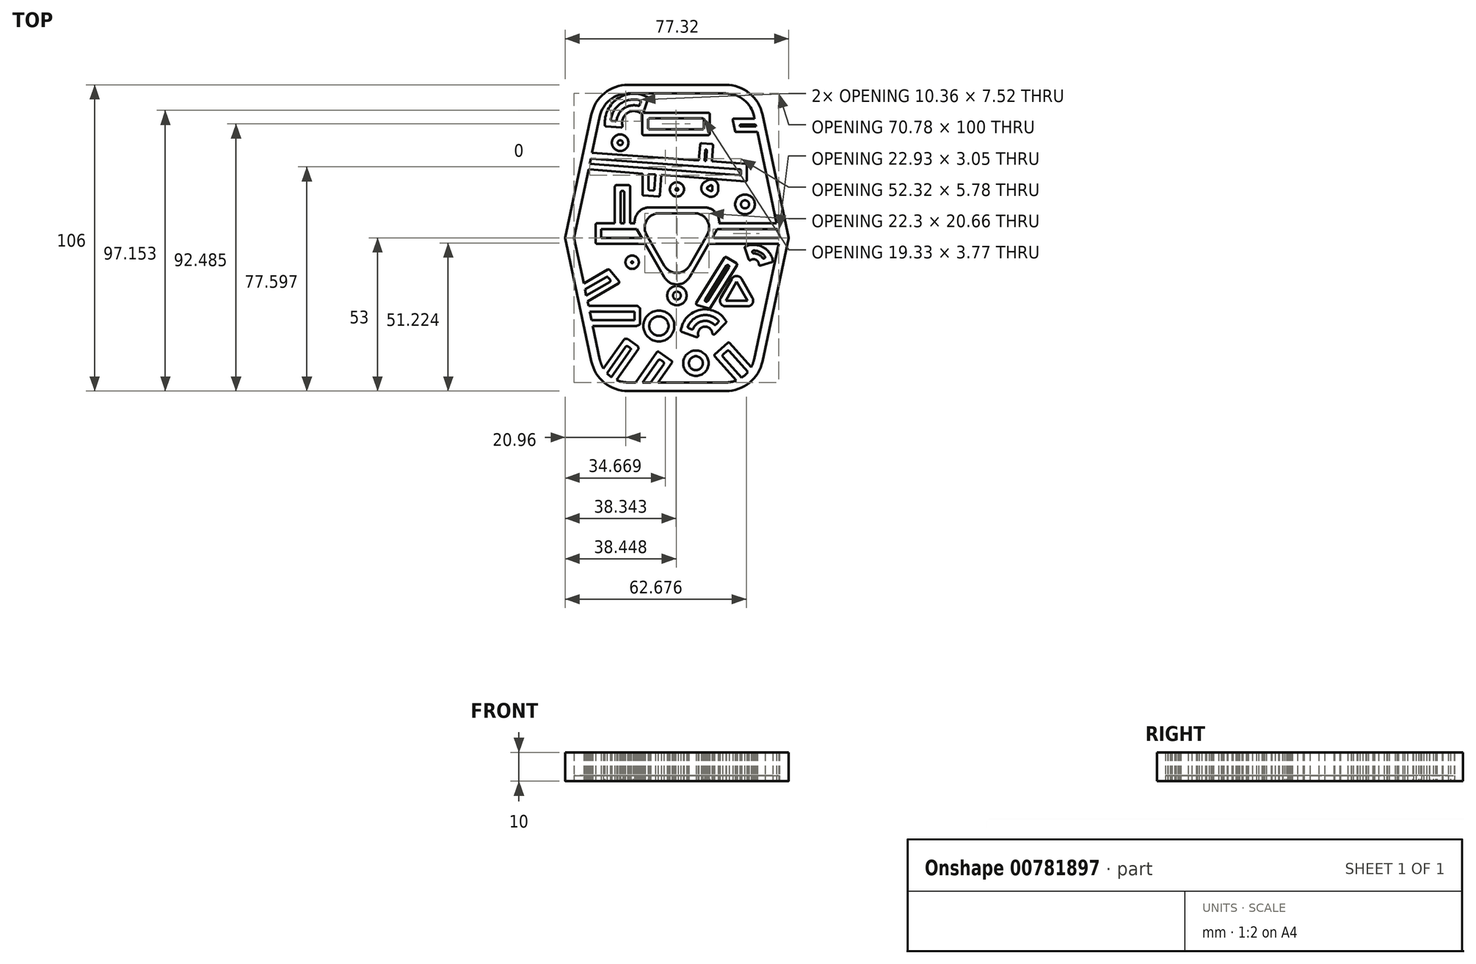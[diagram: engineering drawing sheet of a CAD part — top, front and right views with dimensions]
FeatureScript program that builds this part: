
annotation { "Feature Type Name" : "Feature", "Feature Type Description" : "" }
export const myFeature = defineFeature(function(context is Context, id is Id, definition is map)
    precondition{}
    {
        {
            var Q0;
            Q0=qCreatedBy(makeId("Top.planeOp"),FACE);
            var sketch = newSketch(context, id + "F0", { "sketchPlane" : qUnion([Q0])});
            skPoint(sketch, "E0.orphan", {"position": v(35.6, 0) * mm});
            skPoint(sketch, "E1.visualSharp", {"position": v(35, 0) * mm});
            skPoint(sketch, "E2.visualSharp", {"position": v(-41.06, 0) * mm});
            skArc(sketch, "E3", {"start": v(12.85, -29.92) * mm, "mid": v(8.9, -28.77) * mm, "end": v(5.69, -31.32) * mm});
            skArc(sketch, "E4.0", {"start": v(14.24, -28.47) * mm, "mid": v(8.49, -26.81) * mm, "end": v(3.83, -30.58) * mm});
            skLineSegment(sketch, "E5", {"start": v(4.12, -31.25) * mm, "end": v(5.06, -31.59) * mm});
            skLineSegment(sketch, "E6", {"start": v(14.25, -29.18) * mm, "end": v(13.56, -29.9) * mm});
            skCircle(sketch, "E7.cCircle", {"center": v(0, 0) * mm, "radius": 8.55 * mm, "construction": true});
            skLineSegment(sketch, "E7.0", {"start": v(-6.15, 8.55) * mm, "end": v(6.15, 8.55) * mm});
            skLineSegment(sketch, "E7.1", {"start": v(10.48, 1.05) * mm, "end": v(4.33, -9.6) * mm});
            skLineSegment(sketch, "E7.2", {"start": v(-4.33, -9.6) * mm, "end": v(-10.48, 1.05) * mm});
            skPoint(sketch, "E7.0.midPoint", {"position": v(0, 8.55) * mm});
            skLineSegment(sketch, "E8.0", {"start": v(-9.62, 10.55) * mm, "end": v(9.62, 10.55) * mm});
            skLineSegment(sketch, "E8.1", {"start": v(-4.33, -13.6) * mm, "end": v(-11.03, -2) * mm});
            skLineSegment(sketch, "E8.2", {"start": v(13.8, 2.8) * mm, "end": v(12.62, 0.75) * mm});
            skLineSegment(sketch, "E9", {"start": v(-29.56, -28.5) * mm, "end": v(-14.73, -28.5) * mm});
            skLineSegment(sketch, "E10", {"start": v(-14.73, -28.5) * mm, "end": v(-14.73, -25.54) * mm});
            skLineSegment(sketch, "E11", {"start": v(-14.73, -25.54) * mm, "end": v(-30.19, -25.54) * mm});
            skLineSegment(sketch, "E12.0", {"start": v(-14.73, -23.54) * mm, "end": v(-30.6, -23.54) * mm});
            skLineSegment(sketch, "E13.0", {"start": v(-12.73, -29.9) * mm, "end": v(-12.73, -25.66) * mm});
            skLineSegment(sketch, "E13.1", {"start": v(-29.14, -30.5) * mm, "end": v(-14.16, -30.5) * mm});
            skLineSegment(sketch, "E14", {"start": v(-14.73, -23.54) * mm, "end": v(-13.63, -23.54) * mm});
            skLineSegment(sketch, "E15", {"start": v(-12.76, -24.33) * mm, "end": v(-12.73, -25.66) * mm});
            skArc(sketch, "E16", {"start": v(-12.76, -24.33) * mm, "mid": v(-13.17, -23.91) * mm, "end": v(-13.63, -23.54) * mm});
            skArc(sketch, "E17", {"start": v(-14.16, -30.5) * mm, "mid": v(-13.43, -30.24) * mm, "end": v(-12.73, -29.9) * mm});
            skPoint(sketch, "E18.visualSharp", {"position": v(0, -21.1) * mm});
            skArc(sketch, "E18.filletArc", {"start": v(-4.33, -13.6) * mm, "mid": v(0, -16.1) * mm, "end": v(4.33, -13.6) * mm});
            skPoint(sketch, "E19.visualSharp", {"position": v(0, -17.1) * mm});
            skArc(sketch, "E19.filletArc", {"start": v(-4.33, -9.6) * mm, "mid": v(0, -12.1) * mm, "end": v(4.33, -9.6) * mm});
            skArc(sketch, "E20.filletArc", {"start": v(14.6, 5.05) * mm, "mid": v(13.32, 8.9) * mm, "end": v(9.62, 10.55) * mm});
            skArc(sketch, "E21.filletArc", {"start": v(10.48, 1.05) * mm, "mid": v(10.48, 6.05) * mm, "end": v(6.15, 8.55) * mm});
            skArc(sketch, "E22.filletArc", {"start": v(-9.62, 10.55) * mm, "mid": v(-13.32, 8.9) * mm, "end": v(-14.6, 5.05) * mm});
            skArc(sketch, "E23.filletArc", {"start": v(-6.15, 8.55) * mm, "mid": v(-10.48, 6.05) * mm, "end": v(-10.48, 1.05) * mm});
            skPoint(sketch, "E24.2.start.orphan", {"position": v(-16, 68.56) * mm});
            skLineSegment(sketch, "E25", {"start": v(-13.95, 3.05) * mm, "end": v(-26.18, 3.05) * mm});
            skLineSegment(sketch, "E26", {"start": v(-12.18, 0) * mm, "end": v(-28.18, 0) * mm});
            skLineSegment(sketch, "E27.0", {"start": v(-14.6, 5.05) * mm, "end": v(-16.21, 5.05) * mm});
            skLineSegment(sketch, "E28.0", {"start": v(-12.18, -2) * mm, "end": v(-27.68, -2) * mm});
            skLineSegment(sketch, "E29", {"start": v(-12.18, -2) * mm, "end": v(-11.03, -2) * mm});
            skLineSegment(sketch, "E30", {"start": v(-58.8, 0) * mm, "end": v(-35.6, 0) * mm, "construction": true});
            skLineSegment(sketch, "E31", {"start": v(0, 47.65) * mm, "end": v(0, -85.38) * mm, "construction": true});
            skLineSegment(sketch, "E32", {"start": v(26.68, -42.07) * mm, "end": v(35.18, -2) * mm});
            skLineSegment(sketch, "E33", {"start": v(16.9, -50) * mm, "end": v(0, -50) * mm});
            skPoint(sketch, "E34.visualSharp", {"position": v(25, -50) * mm});
            skArc(sketch, "E34.filletArc", {"start": v(16.9, -50) * mm, "mid": v(18.76, -49.83) * mm, "end": v(20.55, -49.3) * mm});
            skLineSegment(sketch, "E35.MirrorCS", {"start": v(-16.9, -50) * mm, "end": v(-14.28, -50) * mm});
            skArc(sketch, "E36.MirrorCS", {"start": v(-16.9, -50) * mm, "mid": v(-18.95, -49.79) * mm, "end": v(-20.92, -49.15) * mm});
            skLineSegment(sketch, "E37.MirrorCS", {"start": v(-26.68, -42.07) * mm, "end": v(-29.14, -30.5) * mm});
            skLineSegment(sketch, "E38.MirrorCS", {"start": v(26.68, 42.07) * mm, "end": v(26.84, 41.31) * mm});
            skArc(sketch, "E39.MirrorCS", {"start": v(16.9, 50) * mm, "mid": v(23.2, 47.77) * mm, "end": v(26.68, 42.07) * mm});
            skLineSegment(sketch, "E40.MirrorCS", {"start": v(16.9, 50) * mm, "end": v(0, 50) * mm});
            skLineSegment(sketch, "E41.MirrorCS", {"start": v(-16.9, 50) * mm, "end": v(0, 50) * mm});
            skArc(sketch, "E42.MirrorCS", {"start": v(-16.9, 50) * mm, "mid": v(-23.2, 47.77) * mm, "end": v(-26.68, 42.07) * mm});
            skLineSegment(sketch, "E43.MirrorCS", {"start": v(-26.68, 42.07) * mm, "end": v(-29.35, 29.46) * mm});
            skArc(sketch, "E44.0", {"start": v(-16.9, 53) * mm, "mid": v(-25.08, 50.1) * mm, "end": v(-29.62, 42.7) * mm});
            skLineSegment(sketch, "E44.1", {"start": v(29.62, -42.7) * mm, "end": v(38.64, -0.1) * mm});
            skLineSegment(sketch, "E44.2", {"start": v(29.62, 42.7) * mm, "end": v(38.64, 0.1) * mm});
            skArc(sketch, "E44.3", {"start": v(16.9, 53) * mm, "mid": v(25.08, 50.1) * mm, "end": v(29.62, 42.7) * mm});
            skLineSegment(sketch, "E44.4", {"start": v(16.9, 53) * mm, "end": v(0, 53) * mm});
            skArc(sketch, "E44.5", {"start": v(16.9, -53) * mm, "mid": v(25.08, -50.1) * mm, "end": v(29.62, -42.7) * mm});
            skLineSegment(sketch, "E44.6", {"start": v(-16.9, 53) * mm, "end": v(0, 53) * mm});
            skLineSegment(sketch, "E44.7", {"start": v(16.9, -53) * mm, "end": v(0, -53) * mm});
            skLineSegment(sketch, "E44.8", {"start": v(-16.9, -53) * mm, "end": v(0, -53) * mm});
            skArc(sketch, "E44.9", {"start": v(-16.9, -53) * mm, "mid": v(-25.08, -50.1) * mm, "end": v(-29.62, -42.7) * mm});
            skLineSegment(sketch, "E44.10", {"start": v(-29.62, -42.7) * mm, "end": v(-38.64, -0.1) * mm});
            skLineSegment(sketch, "E44.11", {"start": v(-29.62, 42.7) * mm, "end": v(-38.64, 0.1) * mm});
            skLineSegment(sketch, "E45", {"start": v(9.35, 40) * mm, "end": v(9.35, 38.1) * mm});
            skLineSegment(sketch, "E46", {"start": v(8.85, 37.6) * mm, "end": v(-9.48, 37.6) * mm});
            skLineSegment(sketch, "E47", {"start": v(-9.98, 38.1) * mm, "end": v(-9.98, 40.87) * mm});
            skLineSegment(sketch, "E48", {"start": v(-9.48, 41.37) * mm, "end": v(8.85, 41.37) * mm});
            skLineSegment(sketch, "E49", {"start": v(9.35, 40.87) * mm, "end": v(9.35, 40) * mm});
            skLineSegment(sketch, "E50", {"start": v(-22.67, -48.17) * mm, "end": v(-16.9, -40) * mm});
            skPoint(sketch, "E50.startSnap0", {"position": v(-22.67, -23.54) * mm});
            skLineSegment(sketch, "E51.1", {"start": v(-16.97, -37.5) * mm, "end": v(-16.15, -38.08) * mm});
            skLineSegment(sketch, "E51.2", {"start": v(-24.19, -46.85) * mm, "end": v(-17.66, -37.62) * mm});
            skLineSegment(sketch, "E52", {"start": v(-16.9, -40) * mm, "end": v(-16.03, -38.78) * mm});
            skLineSegment(sketch, "E53.0", {"start": v(-21.04, -49.32) * mm, "end": v(-15.26, -41.15) * mm});
            skLineSegment(sketch, "E53.1", {"start": v(-15.26, -41.15) * mm, "end": v(-13.3, -38.39) * mm});
            skLineSegment(sketch, "E53.2", {"start": v(-17.1, -34.96) * mm, "end": v(-13.52, -37.49) * mm});
            skLineSegment(sketch, "E53.3", {"start": v(-25.46, -45.17) * mm, "end": v(-18.25, -34.99) * mm});
            skLineSegment(sketch, "E54", {"start": v(-11.83, -50) * mm, "end": v(-6.41, -42.33) * mm});
            skLineSegment(sketch, "E55", {"start": v(-5.72, -42.21) * mm, "end": v(-4.67, -42.96) * mm});
            skLineSegment(sketch, "E56", {"start": v(-4.55, -43.65) * mm, "end": v(-9.04, -50) * mm});
            skLineSegment(sketch, "E57.0", {"start": v(-1.76, -43.17) * mm, "end": v(-6.59, -50) * mm});
            skLineSegment(sketch, "E57.1", {"start": v(-6.2, -39.43) * mm, "end": v(-1.88, -42.48) * mm});
            skLineSegment(sketch, "E57.2", {"start": v(-13.47, -48.85) * mm, "end": v(-6.9, -39.55) * mm});
            skLineSegment(sketch, "E58", {"start": v(-13.47, -48.85) * mm, "end": v(-14.28, -50) * mm});
            skCircle(sketch, "E59", {"center": v(-6.24, -30.45) * mm, "radius": 3.34 * mm});
            skCircle(sketch, "E60.0", {"center": v(-6.24, -30.45) * mm, "radius": 5.34 * mm});
            skArc(sketch, "E61", {"start": v(-17.1, -34.96) * mm, "mid": v(-17.68, -34.94) * mm, "end": v(-18.25, -34.99) * mm});
            skArc(sketch, "E62", {"start": v(-13.3, -38.39) * mm, "mid": v(-13.37, -37.93) * mm, "end": v(-13.52, -37.49) * mm});
            skArc(sketch, "E63.trimOffspring", {"start": v(-25.46, -45.17) * mm, "mid": v(-26.2, -43.68) * mm, "end": v(-26.68, -42.07) * mm});
            skArc(sketch, "E64.0", {"start": v(16.98, -28.7) * mm, "mid": v(8.04, -24.86) * mm, "end": v(1.38, -31.96) * mm});
            skLineSegment(sketch, "E64.1", {"start": v(16.9, -29.31) * mm, "end": v(13.1, -33.26) * mm});
            skArc(sketch, "E64.2", {"start": v(12.23, -32.96) * mm, "mid": v(9.38, -30.71) * mm, "end": v(7.36, -33.73) * mm});
            skLineSegment(sketch, "E64.3", {"start": v(1.7, -32.5) * mm, "end": v(6.7, -34.31) * mm});
            skCircle(sketch, "E65", {"center": v(6.55, -43.33) * mm, "radius": 2.4 * mm});
            skCircle(sketch, "E66.0", {"center": v(6.55, -43.33) * mm, "radius": 4.4 * mm});
            skLineSegment(sketch, "E67", {"start": v(14.24, 3.05) * mm, "end": v(34.55, 3.05) * mm});
            skLineSegment(sketch, "E68", {"start": v(-9.88, 0) * mm, "end": v(-8.55, 0) * mm});
            skLineSegment(sketch, "E69", {"start": v(-8.72, -2) * mm, "end": v(-8.31, -2) * mm});
            skLineSegment(sketch, "E70.trimOffspring", {"start": v(-9.88, 0) * mm, "end": v(-8.55, 0) * mm, "construction": true});
            skLineSegment(sketch, "E71.trimOffspring", {"start": v(14.6, 5.05) * mm, "end": v(34.53, 5.05) * mm});
            skLineSegment(sketch, "E72.trimOffspring", {"start": v(8.55, 0) * mm, "end": v(9.88, 0) * mm, "construction": true});
            skLineSegment(sketch, "E73.trimOffspring", {"start": v(8.55, 0) * mm, "end": v(9.88, 0) * mm});
            skLineSegment(sketch, "E74.trimOffspring", {"start": v(8.31, -2) * mm, "end": v(8.72, -2) * mm});
            skLineSegment(sketch, "E75.trimOffspring", {"start": v(12.18, 0) * mm, "end": v(60.57, 0) * mm, "construction": true});
            skLineSegment(sketch, "E76.trimOffspring", {"start": v(11.03, -2) * mm, "end": v(35.18, -2) * mm});
            skLineSegment(sketch, "E77.trimOffspring", {"start": v(13.05, 0) * mm, "end": v(34.98, 0) * mm});
            skLineSegment(sketch, "E78", {"start": v(22.39, -48.36) * mm, "end": v(15.9, -41.12) * mm});
            skLineSegment(sketch, "E79", {"start": v(15.94, -40.41) * mm, "end": v(17.39, -39.11) * mm});
            skLineSegment(sketch, "E80", {"start": v(18.1, -39.15) * mm, "end": v(24.58, -46.4) * mm});
            skLineSegment(sketch, "E81.0", {"start": v(18.25, -36.33) * mm, "end": v(25.73, -44.68) * mm});
            skLineSegment(sketch, "E81.1", {"start": v(13.12, -40.25) * mm, "end": v(17.55, -36.29) * mm});
            skLineSegment(sketch, "E81.2", {"start": v(20.55, -49.3) * mm, "end": v(13.08, -40.96) * mm});
            skLineSegment(sketch, "E82.0", {"start": v(11.35, 42.87) * mm, "end": v(11.35, 40) * mm});
            skLineSegment(sketch, "E82.1", {"start": v(-11.65, 43.37) * mm, "end": v(10.85, 43.37) * mm});
            skLineSegment(sketch, "E82.2", {"start": v(11.35, 40) * mm, "end": v(11.35, 36.1) * mm});
            skLineSegment(sketch, "E82.3", {"start": v(10.85, 35.6) * mm, "end": v(-11.48, 35.6) * mm});
            skLineSegment(sketch, "E82.4", {"start": v(-11.98, 36.1) * mm, "end": v(-11.98, 42.72) * mm});
            skCircle(sketch, "E83.cCircle", {"center": v(20.66, -19.5) * mm, "radius": 2.17 * mm, "construction": true});
            skLineSegment(sketch, "E83.0", {"start": v(24.41, -21.68) * mm, "end": v(16.9, -21.68) * mm});
            skLineSegment(sketch, "E83.1", {"start": v(16.9, -21.68) * mm, "end": v(20.66, -15.17) * mm});
            skLineSegment(sketch, "E83.2", {"start": v(20.66, -15.17) * mm, "end": v(24.41, -21.68) * mm});
            skPoint(sketch, "E83.0.midPoint", {"position": v(20.66, -21.68) * mm});
            skLineSegment(sketch, "E84.0", {"start": v(15.17, -20.68) * mm, "end": v(18.92, -14.17) * mm});
            skLineSegment(sketch, "E84.1", {"start": v(24.41, -23.68) * mm, "end": v(16.9, -23.68) * mm});
            skLineSegment(sketch, "E84.2", {"start": v(22.39, -14.17) * mm, "end": v(26.14, -20.68) * mm});
            skPoint(sketch, "E85.visualSharp", {"position": v(20.66, -11.17) * mm});
            skArc(sketch, "E85.filletArc", {"start": v(22.39, -14.17) * mm, "mid": v(20.66, -13.17) * mm, "end": v(18.92, -14.17) * mm});
            skArc(sketch, "E86.filletArc", {"start": v(24.41, -23.68) * mm, "mid": v(26.14, -22.68) * mm, "end": v(26.14, -20.68) * mm});
            skArc(sketch, "E87.filletArc", {"start": v(15.17, -20.68) * mm, "mid": v(15.17, -22.68) * mm, "end": v(16.9, -23.68) * mm});
            skLineSegment(sketch, "E88", {"start": v(-28.18, 4.55) * mm, "end": v(-28.18, -1.5) * mm});
            skLineSegment(sketch, "E89.trimOffspring", {"start": v(-26.18, 0) * mm, "end": v(-12.18, 0) * mm, "construction": true});
            skLineSegment(sketch, "E90.trimOffspring", {"start": v(-31.9, 0) * mm, "end": v(-41.06, 0) * mm});
            skArc(sketch, "E91", {"start": v(29.63, -6.93) * mm, "mid": v(28.3, -5.78) * mm, "end": v(26.58, -5.35) * mm});
            skArc(sketch, "E92.0", {"start": v(30.44, -6.35) * mm, "mid": v(28.75, -4.9) * mm, "end": v(26.6, -4.35) * mm});
            skLineSegment(sketch, "E93", {"start": v(26.11, -5.01) * mm, "end": v(26.11, -5.01) * mm});
            skLineSegment(sketch, "E94", {"start": v(30.18, -7.12) * mm, "end": v(30.18, -7.12) * mm});
            skArc(sketch, "E95.0", {"start": v(33.22, -7.83) * mm, "mid": v(29.68, -3.12) * mm, "end": v(23.78, -2.93) * mm});
            skLineSegment(sketch, "E95.1", {"start": v(32.88, -8.4) * mm, "end": v(29, -9.55) * mm});
            skArc(sketch, "E95.2", {"start": v(28.36, -9.1) * mm, "mid": v(27.37, -7.56) * mm, "end": v(25.55, -7.64) * mm});
            skLineSegment(sketch, "E95.3", {"start": v(23.5, -3.55) * mm, "end": v(24.8, -7.38) * mm});
            skLineSegment(sketch, "E96", {"start": v(10.66, -21.84) * mm, "end": v(18, -10.12) * mm});
            skLineSegment(sketch, "E97", {"start": v(17.84, -9.43) * mm, "end": v(17.83, -9.42) * mm});
            skLineSegment(sketch, "E98", {"start": v(17.14, -9.58) * mm, "end": v(9.8, -21.3) * mm});
            skLineSegment(sketch, "E99", {"start": v(10.07, -22.04) * mm, "end": v(10.08, -22.05) * mm});
            skLineSegment(sketch, "E100.0", {"start": v(11.53, -24.2) * mm, "end": v(20.76, -9.5) * mm});
            skLineSegment(sketch, "E100.1", {"start": v(7, -23.18) * mm, "end": v(10.96, -24.42) * mm});
            skLineSegment(sketch, "E100.2", {"start": v(16.5, -6.83) * mm, "end": v(6.72, -22.44) * mm});
            skLineSegment(sketch, "E100.3", {"start": v(20.6, -8.8) * mm, "end": v(17.2, -6.67) * mm});
            skCircle(sketch, "E101", {"center": v(0, -19.95) * mm, "radius": 1.36 * mm});
            skCircle(sketch, "E102.0", {"center": v(0, -19.95) * mm, "radius": 3.36 * mm});
            skLineSegment(sketch, "E103", {"start": v(-31.38, -19.9) * mm, "end": v(-23.24, -15.2) * mm});
            skLineSegment(sketch, "E104", {"start": v(-23.1, -14.44) * mm, "end": v(-23.76, -13.66) * mm});
            skLineSegment(sketch, "E105", {"start": v(-24.4, -13.55) * mm, "end": v(-31.82, -17.83) * mm});
            skLineSegment(sketch, "E106.0", {"start": v(-23.93, -10.97) * mm, "end": v(-32.26, -15.78) * mm});
            skLineSegment(sketch, "E106.1", {"start": v(-20.06, -15) * mm, "end": v(-23.3, -11.08) * mm});
            skLineSegment(sketch, "E106.2", {"start": v(-30.38, -21.63) * mm, "end": v(-20.2, -15.74) * mm});
            skLineSegment(sketch, "E107", {"start": v(-30.38, -21.63) * mm, "end": v(-30.95, -21.95) * mm});
            skCircle(sketch, "E108", {"center": v(-15.5, -8.41) * mm, "radius": 0.31 * mm});
            skCircle(sketch, "E109.0", {"center": v(-15.5, -8.41) * mm, "radius": 2.31 * mm});
            skLineSegment(sketch, "E110", {"start": v(-29.77, 27.49) * mm, "end": v(21.7, 23.8) * mm});
            skLineSegment(sketch, "E111", {"start": v(22.17, 23.3) * mm, "end": v(22.17, 22.2) * mm});
            skLineSegment(sketch, "E112", {"start": v(21.63, 21.7) * mm, "end": v(-30.15, 25.7) * mm});
            skLineSegment(sketch, "E113.0", {"start": v(23.63, 19.55) * mm, "end": v(-5.4, 21.8) * mm});
            skLineSegment(sketch, "E113.1", {"start": v(24.17, 25.17) * mm, "end": v(24.17, 20.05) * mm});
            skLineSegment(sketch, "E113.2", {"start": v(-29.63, 29.48) * mm, "end": v(7.6, 26.82) * mm});
            skLineSegment(sketch, "E114.bottom", {"start": v(-18.21, 5.05) * mm, "end": v(-19.46, 5.05) * mm});
            skLineSegment(sketch, "E114.top", {"start": v(-18.71, 16.26) * mm, "end": v(-18.96, 16.26) * mm});
            skLineSegment(sketch, "E114.left", {"start": v(-18.21, 5.05) * mm, "end": v(-18.21, 15.76) * mm});
            skLineSegment(sketch, "E114.right", {"start": v(-19.46, 5.05) * mm, "end": v(-19.46, 15.76) * mm});
            skLineSegment(sketch, "E115.0", {"start": v(-21.46, 5.05) * mm, "end": v(-21.46, 17.76) * mm});
            skLineSegment(sketch, "E115.1", {"start": v(-16.71, 18.26) * mm, "end": v(-20.96, 18.26) * mm});
            skLineSegment(sketch, "E115.2", {"start": v(-16.21, 5.05) * mm, "end": v(-16.21, 17.76) * mm});
            skLineSegment(sketch, "E116.trimOffspring", {"start": v(-21.46, 5.05) * mm, "end": v(-27.68, 5.05) * mm});
            skArc(sketch, "E117.trimOffspring", {"start": v(-22.67, -48.17) * mm, "mid": v(-23.46, -47.54) * mm, "end": v(-24.19, -46.85) * mm});
            skLineSegment(sketch, "E118.trimOffspring", {"start": v(-29.56, -28.5) * mm, "end": v(-30.19, -25.54) * mm});
            skLineSegment(sketch, "E119.trimOffspring", {"start": v(-30.6, -23.54) * mm, "end": v(-30.95, -21.95) * mm});
            skLineSegment(sketch, "E120.trimOffspring", {"start": v(-31.38, -19.9) * mm, "end": v(-31.82, -17.83) * mm});
            skLineSegment(sketch, "E121.trimOffspring", {"start": v(-32.26, -15.78) * mm, "end": v(-35.18, -2) * mm});
            skLineSegment(sketch, "E122.trimOffspring", {"start": v(-34.95, 3.05) * mm, "end": v(-35.6, 0) * mm});
            skPoint(sketch, "E123.orphan", {"position": v(-35.6, 0) * mm});
            skLineSegment(sketch, "E124.trimOffspring", {"start": v(-12.18, 0) * mm, "end": v(-13.95, 3.05) * mm});
            skLineSegment(sketch, "E125.trimOffspring", {"start": v(11.03, -2) * mm, "end": v(4.33, -13.6) * mm});
            skLineSegment(sketch, "E126", {"start": v(-30.3, 23.71) * mm, "end": v(-30.56, 23.77) * mm});
            skPoint(sketch, "E126.endSnap0", {"position": v(-30.6, 23.56) * mm});
            skPoint(sketch, "E127.orphan", {"position": v(-30.6, 23.78) * mm});
            skLineSegment(sketch, "E128.trimOffspring", {"start": v(-29.77, 27.49) * mm, "end": v(-30.15, 25.7) * mm});
            skLineSegment(sketch, "E129.trimOffspring", {"start": v(-30.56, 23.77) * mm, "end": v(-34.53, 5.05) * mm});
            skLineSegment(sketch, "E130.trimOffspring", {"start": v(35.04, 2.66) * mm, "end": v(35.47, 0.6) * mm});
            skLineSegment(sketch, "E131", {"start": v(-9.9, 22.14) * mm, "end": v(-9.9, 17.04) * mm});
            skLineSegment(sketch, "E132", {"start": v(-9.44, 16.54) * mm, "end": v(-8.32, 16.45) * mm});
            skLineSegment(sketch, "E133", {"start": v(-7.78, 16.91) * mm, "end": v(-7.4, 21.94) * mm});
            skLineSegment(sketch, "E134.0", {"start": v(-5.94, 14.76) * mm, "end": v(-5.4, 21.8) * mm});
            skLineSegment(sketch, "E134.1", {"start": v(-11.44, 14.69) * mm, "end": v(-6.48, 14.3) * mm});
            skLineSegment(sketch, "E134.2", {"start": v(-11.9, 22.3) * mm, "end": v(-11.9, 15.19) * mm});
            skCircle(sketch, "E135", {"center": v(23.57, 11.64) * mm, "radius": 1.4 * mm});
            skCircle(sketch, "E136.0", {"center": v(23.57, 11.64) * mm, "radius": 3.4 * mm});
            skCircle(sketch, "E137", {"center": v(0, 16.81) * mm, "radius": 0.47 * mm});
            skCircle(sketch, "E138.0", {"center": v(0, 16.81) * mm, "radius": 2.47 * mm});
            skPoint(sketch, "E139", {"position": v(0, 10.55) * mm});
            skCircle(sketch, "E140.cCircle", {"center": v(11.51, 17.23) * mm, "radius": 0.8 * mm, "construction": true});
            skLineSegment(sketch, "E140.0", {"start": v(10.69, 17.68) * mm, "end": v(11.57, 18.17) * mm});
            skLineSegment(sketch, "E140.1", {"start": v(12.31, 17.72) * mm, "end": v(12.3, 16.71) * mm});
            skLineSegment(sketch, "E140.2", {"start": v(11.54, 16.3) * mm, "end": v(10.67, 16.81) * mm});
            skPoint(sketch, "E140.0.midPoint", {"position": v(11.13, 17.92) * mm});
            skPoint(sketch, "E141.visualSharp", {"position": v(12.33, 18.59) * mm});
            skArc(sketch, "E141.filletArc", {"start": v(12.31, 17.72) * mm, "mid": v(12.07, 18.16) * mm, "end": v(11.57, 18.17) * mm});
            skPoint(sketch, "E142.visualSharp", {"position": v(12.28, 15.85) * mm});
            skArc(sketch, "E142.filletArc", {"start": v(11.54, 16.3) * mm, "mid": v(12.04, 16.28) * mm, "end": v(12.3, 16.71) * mm});
            skPoint(sketch, "E143.visualSharp", {"position": v(9.93, 17.26) * mm});
            skArc(sketch, "E143.filletArc", {"start": v(10.69, 17.68) * mm, "mid": v(10.43, 17.25) * mm, "end": v(10.67, 16.81) * mm});
            skArc(sketch, "E144.0", {"start": v(14.31, 17.69) * mm, "mid": v(13.1, 19.87) * mm, "end": v(10.6, 19.92) * mm});
            skArc(sketch, "E144.1", {"start": v(10.51, 14.58) * mm, "mid": v(13, 14.54) * mm, "end": v(14.3, 16.68) * mm});
            skLineSegment(sketch, "E144.2", {"start": v(10.51, 14.58) * mm, "end": v(9.65, 15.1) * mm});
            skLineSegment(sketch, "E144.3", {"start": v(14.31, 17.69) * mm, "end": v(14.3, 16.68) * mm});
            skArc(sketch, "E144.4", {"start": v(9.72, 19.43) * mm, "mid": v(8.43, 17.28) * mm, "end": v(9.65, 15.1) * mm});
            skLineSegment(sketch, "E144.5", {"start": v(9.72, 19.43) * mm, "end": v(10.6, 19.92) * mm});
            skArc(sketch, "E145.MirrorCS", {"start": v(-20.89, 40.81) * mm, "mid": v(-18.25, 44.9) * mm, "end": v(-13.45, 45.75) * mm});
            skArc(sketch, "E146.MirrorCS", {"start": v(-18.85, 38.85) * mm, "mid": v(-16.89, 43.4) * mm, "end": v(-11.98, 42.72) * mm});
            skLineSegment(sketch, "E147.MirrorCS", {"start": v(-24.48, 38.62) * mm, "end": v(-19.37, 38.23) * mm});
            skArc(sketch, "E148.MirrorCS", {"start": v(-24.94, 39.09) * mm, "mid": v(-20.28, 48.35) * mm, "end": v(-9.9, 48.61) * mm});
            skArc(sketch, "E149.MirrorCS", {"start": v(-22.88, 41.04) * mm, "mid": v(-19.35, 46.57) * mm, "end": v(-12.9, 47.67) * mm});
            skLineSegment(sketch, "E150.MirrorCS", {"start": v(-9.9, 48.61) * mm, "end": v(-11.65, 43.37) * mm});
            skLineSegment(sketch, "E151.MirrorCS", {"start": v(-12.54, 47.03) * mm, "end": v(-12.86, 46.08) * mm});
            skLineSegment(sketch, "E152.MirrorCS", {"start": v(-22.42, 40.47) * mm, "end": v(-21.42, 40.4) * mm});
            skPoint(sketch, "E153.start.orphan", {"position": v(22.94, 40.51) * mm});
            skPoint(sketch, "E154.1.start.orphan", {"position": v(24.9, 38.66) * mm});
            skPoint(sketch, "E155.start.orphan", {"position": v(20.95, 40.36) * mm});
            skPoint(sketch, "E154.2.end.orphan", {"position": v(11.9, 42.63) * mm});
            skLineSegment(sketch, "E156", {"start": v(26.86, 39.31) * mm, "end": v(22.3, 39.31) * mm});
            skLineSegment(sketch, "E157", {"start": v(21.8, 38.7) * mm, "end": v(21.81, 38.66) * mm});
            skLineSegment(sketch, "E158", {"start": v(21.81, 38.66) * mm, "end": v(27.4, 38.66) * mm});
            skLineSegment(sketch, "E159.0", {"start": v(20.6, 36.66) * mm, "end": v(27.4, 36.66) * mm});
            skLineSegment(sketch, "E159.1", {"start": v(19.33, 40.7) * mm, "end": v(20.1, 37.05) * mm});
            skLineSegment(sketch, "E159.2", {"start": v(26.84, 41.31) * mm, "end": v(19.82, 41.31) * mm});
            skLineSegment(sketch, "E160", {"start": v(27.4, 36.66) * mm, "end": v(27.81, 36.74) * mm});
            skLineSegment(sketch, "E161.trimOffspring", {"start": v(27.35, 38.92) * mm, "end": v(27.4, 38.66) * mm});
            skLineSegment(sketch, "E162.trimOffspring", {"start": v(27.81, 36.74) * mm, "end": v(34.53, 5.05) * mm});
            skPoint(sketch, "E163.visualSharp", {"position": v(-23.57, -10.76) * mm});
            skArc(sketch, "E163.filletArc", {"start": v(-23.3, -11.08) * mm, "mid": v(-23.6, -10.91) * mm, "end": v(-23.93, -10.97) * mm});
            skPoint(sketch, "E164.visualSharp", {"position": v(-19.68, -15.45) * mm});
            skArc(sketch, "E164.filletArc", {"start": v(-20.2, -15.74) * mm, "mid": v(-19.95, -15.4) * mm, "end": v(-20.06, -15) * mm});
            skPoint(sketch, "E165.visualSharp", {"position": v(-24.03, -13.33) * mm});
            skArc(sketch, "E165.filletArc", {"start": v(-23.76, -13.66) * mm, "mid": v(-24.06, -13.49) * mm, "end": v(-24.4, -13.55) * mm});
            skPoint(sketch, "E166.visualSharp", {"position": v(-22.73, -14.9) * mm});
            skArc(sketch, "E166.filletArc", {"start": v(-23.24, -15.2) * mm, "mid": v(-23, -14.85) * mm, "end": v(-23.1, -14.44) * mm});
            skPoint(sketch, "E167.visualSharp", {"position": v(16.77, -6.4) * mm});
            skArc(sketch, "E167.filletArc", {"start": v(17.2, -6.67) * mm, "mid": v(16.82, -6.6) * mm, "end": v(16.5, -6.83) * mm});
            skPoint(sketch, "E168.visualSharp", {"position": v(17.4, -9.16) * mm});
            skArc(sketch, "E168.filletArc", {"start": v(17.83, -9.42) * mm, "mid": v(17.45, -9.36) * mm, "end": v(17.14, -9.58) * mm});
            skPoint(sketch, "E169.visualSharp", {"position": v(18.27, -9.7) * mm});
            skArc(sketch, "E169.filletArc", {"start": v(18, -10.12) * mm, "mid": v(18.06, -9.75) * mm, "end": v(17.84, -9.43) * mm});
            skPoint(sketch, "E170.visualSharp", {"position": v(21.02, -9.07) * mm});
            skArc(sketch, "E170.filletArc", {"start": v(20.76, -9.5) * mm, "mid": v(20.82, -9.11) * mm, "end": v(20.6, -8.8) * mm});
            skPoint(sketch, "E171.visualSharp", {"position": v(9.45, -21.85) * mm});
            skArc(sketch, "E171.filletArc", {"start": v(9.8, -21.3) * mm, "mid": v(9.75, -21.74) * mm, "end": v(10.07, -22.04) * mm});
            skPoint(sketch, "E172.visualSharp", {"position": v(10.45, -22.16) * mm});
            skArc(sketch, "E172.filletArc", {"start": v(10.08, -22.05) * mm, "mid": v(10.4, -22.04) * mm, "end": v(10.66, -21.84) * mm});
            skPoint(sketch, "E173.visualSharp", {"position": v(6.37, -22.99) * mm});
            skArc(sketch, "E173.filletArc", {"start": v(6.72, -22.44) * mm, "mid": v(6.67, -22.87) * mm, "end": v(7, -23.18) * mm});
            skPoint(sketch, "E174.visualSharp", {"position": v(11.33, -24.53) * mm});
            skArc(sketch, "E174.filletArc", {"start": v(10.96, -24.42) * mm, "mid": v(11.28, -24.4) * mm, "end": v(11.53, -24.2) * mm});
            skPoint(sketch, "E175.visualSharp", {"position": v(23.37, -3.13) * mm});
            skArc(sketch, "E175.filletArc", {"start": v(23.78, -2.93) * mm, "mid": v(23.52, -3.18) * mm, "end": v(23.5, -3.55) * mm});
            skPoint(sketch, "E176.visualSharp", {"position": v(25.05, -8.1) * mm});
            skArc(sketch, "E176.filletArc", {"start": v(24.8, -7.38) * mm, "mid": v(25.11, -7.69) * mm, "end": v(25.55, -7.64) * mm});
            skPoint(sketch, "E177.visualSharp", {"position": v(28.26, -9.77) * mm});
            skArc(sketch, "E177.filletArc", {"start": v(28.36, -9.1) * mm, "mid": v(28.57, -9.48) * mm, "end": v(29, -9.55) * mm});
            skPoint(sketch, "E178.visualSharp", {"position": v(33.3, -8.28) * mm});
            skArc(sketch, "E178.filletArc", {"start": v(32.88, -8.4) * mm, "mid": v(33.16, -8.19) * mm, "end": v(33.22, -7.83) * mm});
            skPoint(sketch, "E179.visualSharp", {"position": v(30.8, -6.93) * mm});
            skArc(sketch, "E179.filletArc", {"start": v(30.18, -7.12) * mm, "mid": v(30.5, -6.8) * mm, "end": v(30.44, -6.35) * mm});
            skPoint(sketch, "E180.visualSharp", {"position": v(29.82, -7.22) * mm});
            skArc(sketch, "E180.filletArc", {"start": v(29.63, -6.93) * mm, "mid": v(29.88, -7.11) * mm, "end": v(30.18, -7.12) * mm});
            skPoint(sketch, "E181.visualSharp", {"position": v(26.23, -5.36) * mm});
            skArc(sketch, "E181.filletArc", {"start": v(26.11, -5.01) * mm, "mid": v(26.3, -5.25) * mm, "end": v(26.58, -5.35) * mm});
            skPoint(sketch, "E182.visualSharp", {"position": v(25.9, -4.4) * mm});
            skArc(sketch, "E182.filletArc", {"start": v(26.6, -4.35) * mm, "mid": v(26.18, -4.56) * mm, "end": v(26.11, -5.01) * mm});
            skPoint(sketch, "E183.visualSharp", {"position": v(17.92, -35.96) * mm});
            skArc(sketch, "E183.filletArc", {"start": v(18.25, -36.33) * mm, "mid": v(17.9, -36.16) * mm, "end": v(17.55, -36.29) * mm});
            skPoint(sketch, "E184.visualSharp", {"position": v(17.76, -38.78) * mm});
            skArc(sketch, "E184.filletArc", {"start": v(18.1, -39.15) * mm, "mid": v(17.75, -38.99) * mm, "end": v(17.39, -39.11) * mm});
            skArc(sketch, "E185.trimOffspring", {"start": v(25.73, -44.68) * mm, "mid": v(26.3, -43.41) * mm, "end": v(26.68, -42.07) * mm});
            skArc(sketch, "E186.trimOffspring", {"start": v(22.39, -48.36) * mm, "mid": v(23.56, -47.46) * mm, "end": v(24.58, -46.4) * mm});
            skPoint(sketch, "E187.visualSharp", {"position": v(-6.6, -39.14) * mm});
            skArc(sketch, "E187.filletArc", {"start": v(-6.2, -39.43) * mm, "mid": v(-6.57, -39.34) * mm, "end": v(-6.9, -39.55) * mm});
            skPoint(sketch, "E188.visualSharp", {"position": v(-1.47, -42.77) * mm});
            skArc(sketch, "E188.filletArc", {"start": v(-1.76, -43.17) * mm, "mid": v(-1.68, -42.8) * mm, "end": v(-1.88, -42.48) * mm});
            skPoint(sketch, "E189.visualSharp", {"position": v(-4.26, -43.24) * mm});
            skArc(sketch, "E189.filletArc", {"start": v(-4.55, -43.65) * mm, "mid": v(-4.46, -43.28) * mm, "end": v(-4.67, -42.96) * mm});
            skPoint(sketch, "E190.visualSharp", {"position": v(-6.12, -41.93) * mm});
            skArc(sketch, "E190.filletArc", {"start": v(-5.72, -42.21) * mm, "mid": v(-6.09, -42.13) * mm, "end": v(-6.41, -42.33) * mm});
            skPoint(sketch, "E191.visualSharp", {"position": v(-17.38, -37.21) * mm});
            skArc(sketch, "E191.filletArc", {"start": v(-16.97, -37.5) * mm, "mid": v(-17.34, -37.42) * mm, "end": v(-17.66, -37.62) * mm});
            skPoint(sketch, "E192.visualSharp", {"position": v(-15.74, -38.37) * mm});
            skArc(sketch, "E192.filletArc", {"start": v(-16.03, -38.78) * mm, "mid": v(-15.95, -38.4) * mm, "end": v(-16.15, -38.08) * mm});
            skPoint(sketch, "E193.visualSharp", {"position": v(24.17, 19.5) * mm});
            skArc(sketch, "E193.filletArc", {"start": v(23.63, 19.55) * mm, "mid": v(24, 19.68) * mm, "end": v(24.17, 20.05) * mm});
            skPoint(sketch, "E194.visualSharp", {"position": v(24.17, 25.63) * mm});
            skArc(sketch, "E194.filletArc", {"start": v(24.17, 25.17) * mm, "mid": v(24.03, 25.5) * mm, "end": v(23.7, 25.66) * mm});
            skPoint(sketch, "E195.visualSharp", {"position": v(22.17, 23.77) * mm});
            skArc(sketch, "E195.filletArc", {"start": v(22.17, 23.3) * mm, "mid": v(22.03, 23.64) * mm, "end": v(21.7, 23.8) * mm});
            skPoint(sketch, "E196.visualSharp", {"position": v(22.17, 21.67) * mm});
            skArc(sketch, "E196.filletArc", {"start": v(21.63, 21.7) * mm, "mid": v(22, 21.84) * mm, "end": v(22.17, 22.2) * mm});
            skLineSegment(sketch, "E197", {"start": v(10.12, 26.64) * mm, "end": v(10.37, 30.12) * mm});
            skLineSegment(sketch, "E198", {"start": v(9.9, 30.65) * mm, "end": v(9.88, 30.66) * mm});
            skLineSegment(sketch, "E199", {"start": v(9.88, 30.66) * mm, "end": v(9.6, 26.67) * mm});
            skLineSegment(sketch, "E200.0", {"start": v(8, 32.3) * mm, "end": v(7.6, 26.82) * mm});
            skLineSegment(sketch, "E200.1", {"start": v(12.04, 32.5) * mm, "end": v(8.53, 32.76) * mm});
            skLineSegment(sketch, "E200.2", {"start": v(12.11, 26.5) * mm, "end": v(12.5, 31.97) * mm});
            skCircle(sketch, "E201", {"center": v(-19.63, 32.96) * mm, "radius": 0.87 * mm});
            skCircle(sketch, "E202.0", {"center": v(-19.63, 32.96) * mm, "radius": 2.87 * mm});
            skPoint(sketch, "E203.start.orphan", {"position": v(-12.73, -27.79) * mm});
            skPoint(sketch, "E204.orphan", {"position": v(-11.9, 42.63) * mm});
            skPoint(sketch, "E205.visualSharp", {"position": v(-9.98, 37.6) * mm});
            skArc(sketch, "E205.filletArc", {"start": v(-9.98, 38.1) * mm, "mid": v(-9.84, 37.75) * mm, "end": v(-9.48, 37.6) * mm});
            skPoint(sketch, "E206.visualSharp", {"position": v(-9.98, 41.37) * mm});
            skArc(sketch, "E206.filletArc", {"start": v(-9.48, 41.37) * mm, "mid": v(-9.84, 41.22) * mm, "end": v(-9.98, 40.87) * mm});
            skPoint(sketch, "E207.visualSharp", {"position": v(9.35, 41.37) * mm});
            skArc(sketch, "E207.filletArc", {"start": v(9.35, 40.87) * mm, "mid": v(9.2, 41.22) * mm, "end": v(8.85, 41.37) * mm});
            skPoint(sketch, "E208.visualSharp", {"position": v(9.35, 37.6) * mm});
            skArc(sketch, "E208.filletArc", {"start": v(8.85, 37.6) * mm, "mid": v(9.2, 37.75) * mm, "end": v(9.35, 38.1) * mm});
            skPoint(sketch, "E209.visualSharp", {"position": v(11.35, 35.6) * mm});
            skArc(sketch, "E209.filletArc", {"start": v(10.85, 35.6) * mm, "mid": v(11.2, 35.75) * mm, "end": v(11.35, 36.1) * mm});
            skPoint(sketch, "E210.visualSharp", {"position": v(11.35, 43.37) * mm});
            skArc(sketch, "E210.filletArc", {"start": v(11.35, 42.87) * mm, "mid": v(11.2, 43.22) * mm, "end": v(10.85, 43.37) * mm});
            skPoint(sketch, "E211.visualSharp", {"position": v(-11.98, 35.6) * mm});
            skArc(sketch, "E211.filletArc", {"start": v(-11.98, 36.1) * mm, "mid": v(-11.84, 35.75) * mm, "end": v(-11.48, 35.6) * mm});
            skPoint(sketch, "E212.visualSharp", {"position": v(21.67, 39.31) * mm});
            skArc(sketch, "E212.filletArc", {"start": v(22.3, 39.31) * mm, "mid": v(21.9, 39.13) * mm, "end": v(21.8, 38.7) * mm});
            skPoint(sketch, "E213.visualSharp", {"position": v(27.27, 39.31) * mm});
            skArc(sketch, "E213.filletArc", {"start": v(27.35, 38.92) * mm, "mid": v(27.18, 39.2) * mm, "end": v(26.86, 39.31) * mm});
            skPoint(sketch, "E214.visualSharp", {"position": v(19.2, 41.31) * mm});
            skArc(sketch, "E214.filletArc", {"start": v(19.82, 41.31) * mm, "mid": v(19.43, 41.13) * mm, "end": v(19.33, 40.7) * mm});
            skPoint(sketch, "E215.visualSharp", {"position": v(20.2, 36.66) * mm});
            skArc(sketch, "E215.filletArc", {"start": v(20.1, 37.05) * mm, "mid": v(20.28, 36.77) * mm, "end": v(20.6, 36.66) * mm});
            skPoint(sketch, "E216.visualSharp", {"position": v(-16.21, 18.26) * mm});
            skArc(sketch, "E216.filletArc", {"start": v(-16.21, 17.76) * mm, "mid": v(-16.36, 18.12) * mm, "end": v(-16.71, 18.26) * mm});
            skPoint(sketch, "E217.visualSharp", {"position": v(-21.46, 18.26) * mm});
            skArc(sketch, "E217.filletArc", {"start": v(-20.96, 18.26) * mm, "mid": v(-21.32, 18.12) * mm, "end": v(-21.46, 17.76) * mm});
            skPoint(sketch, "E218.visualSharp", {"position": v(-19.46, 16.26) * mm});
            skArc(sketch, "E218.filletArc", {"start": v(-18.96, 16.26) * mm, "mid": v(-19.32, 16.12) * mm, "end": v(-19.46, 15.76) * mm});
            skPoint(sketch, "E219.visualSharp", {"position": v(-18.21, 16.26) * mm});
            skArc(sketch, "E219.filletArc", {"start": v(-18.21, 15.76) * mm, "mid": v(-18.36, 16.12) * mm, "end": v(-18.71, 16.26) * mm});
            skPoint(sketch, "E220.visualSharp", {"position": v(13.95, 3.05) * mm});
            skArc(sketch, "E220.filletArc", {"start": v(14.24, 3.05) * mm, "mid": v(13.99, 2.99) * mm, "end": v(13.8, 2.8) * mm});
            skPoint(sketch, "E221.visualSharp", {"position": v(12.18, 0) * mm});
            skArc(sketch, "E221.filletArc", {"start": v(12.62, 0.75) * mm, "mid": v(12.62, 0.25) * mm, "end": v(13.05, 0) * mm});
            skPoint(sketch, "E222.visualSharp", {"position": v(34.95, 3.05) * mm});
            skArc(sketch, "E222.filletArc", {"start": v(35.04, 2.66) * mm, "mid": v(34.86, 2.94) * mm, "end": v(34.55, 3.05) * mm});
            skArc(sketch, "E223.filletArc", {"start": v(34.98, 0) * mm, "mid": v(35.37, 0.19) * mm, "end": v(35.47, 0.6) * mm});
            skPoint(sketch, "E224.visualSharp", {"position": v(-7.82, 16.41) * mm});
            skArc(sketch, "E224.filletArc", {"start": v(-8.32, 16.45) * mm, "mid": v(-7.96, 16.57) * mm, "end": v(-7.78, 16.91) * mm});
            skPoint(sketch, "E225.visualSharp", {"position": v(-9.9, 16.57) * mm});
            skArc(sketch, "E225.filletArc", {"start": v(-9.9, 17.04) * mm, "mid": v(-9.77, 16.7) * mm, "end": v(-9.44, 16.54) * mm});
            skPoint(sketch, "E226.visualSharp", {"position": v(-11.9, 14.72) * mm});
            skArc(sketch, "E226.filletArc", {"start": v(-11.9, 15.19) * mm, "mid": v(-11.77, 14.85) * mm, "end": v(-11.44, 14.69) * mm});
            skPoint(sketch, "E227.visualSharp", {"position": v(-5.98, 14.27) * mm});
            skArc(sketch, "E227.filletArc", {"start": v(-6.48, 14.3) * mm, "mid": v(-6.12, 14.42) * mm, "end": v(-5.94, 14.76) * mm});
            skPoint(sketch, "E228.visualSharp", {"position": v(10.4, 30.62) * mm});
            skArc(sketch, "E228.filletArc", {"start": v(10.37, 30.12) * mm, "mid": v(10.25, 30.48) * mm, "end": v(9.9, 30.65) * mm});
            skPoint(sketch, "E229.visualSharp", {"position": v(12.54, 32.47) * mm});
            skArc(sketch, "E229.filletArc", {"start": v(12.5, 31.97) * mm, "mid": v(12.38, 32.34) * mm, "end": v(12.04, 32.5) * mm});
            skPoint(sketch, "E230.visualSharp", {"position": v(8.03, 32.8) * mm});
            skArc(sketch, "E230.filletArc", {"start": v(8.53, 32.76) * mm, "mid": v(8.17, 32.64) * mm, "end": v(8, 32.3) * mm});
            skPoint(sketch, "E231.visualSharp", {"position": v(-18.62, 38.17) * mm});
            skArc(sketch, "E231.filletArc", {"start": v(-19.37, 38.23) * mm, "mid": v(-18.95, 38.4) * mm, "end": v(-18.85, 38.85) * mm});
            skPoint(sketch, "E232.visualSharp", {"position": v(-24.9, 38.66) * mm});
            skArc(sketch, "E232.filletArc", {"start": v(-24.94, 39.09) * mm, "mid": v(-24.8, 38.77) * mm, "end": v(-24.48, 38.62) * mm});
            skPoint(sketch, "E233.visualSharp", {"position": v(-20.95, 40.36) * mm});
            skArc(sketch, "E233.filletArc", {"start": v(-21.42, 40.4) * mm, "mid": v(-21.07, 40.5) * mm, "end": v(-20.89, 40.81) * mm});
            skPoint(sketch, "E234.visualSharp", {"position": v(-22.94, 40.51) * mm});
            skArc(sketch, "E234.filletArc", {"start": v(-22.88, 41.04) * mm, "mid": v(-22.77, 40.66) * mm, "end": v(-22.42, 40.47) * mm});
            skPoint(sketch, "E235.visualSharp", {"position": v(-12.38, 47.52) * mm});
            skArc(sketch, "E235.filletArc", {"start": v(-12.54, 47.03) * mm, "mid": v(-12.58, 47.43) * mm, "end": v(-12.9, 47.67) * mm});
            skPoint(sketch, "E236.visualSharp", {"position": v(-13, 45.63) * mm});
            skArc(sketch, "E236.filletArc", {"start": v(-13.45, 45.75) * mm, "mid": v(-13.1, 45.8) * mm, "end": v(-12.86, 46.08) * mm});
            skPoint(sketch, "E237.visualSharp", {"position": v(13.2, -30.28) * mm});
            skArc(sketch, "E237.filletArc", {"start": v(12.85, -29.92) * mm, "mid": v(13.2, -30.06) * mm, "end": v(13.56, -29.9) * mm});
            skPoint(sketch, "E238.visualSharp", {"position": v(5.52, -31.75) * mm});
            skArc(sketch, "E238.filletArc", {"start": v(5.06, -31.59) * mm, "mid": v(5.43, -31.58) * mm, "end": v(5.69, -31.32) * mm});
            skPoint(sketch, "E239.visualSharp", {"position": v(3.64, -31.07) * mm});
            skArc(sketch, "E239.filletArc", {"start": v(3.83, -30.58) * mm, "mid": v(3.83, -30.97) * mm, "end": v(4.12, -31.25) * mm});
            skPoint(sketch, "E240.visualSharp", {"position": v(14.59, -28.84) * mm});
            skArc(sketch, "E240.filletArc", {"start": v(14.25, -29.18) * mm, "mid": v(14.4, -28.83) * mm, "end": v(14.24, -28.47) * mm});
            skPoint(sketch, "E241.visualSharp", {"position": v(17.17, -29.04) * mm});
            skArc(sketch, "E241.filletArc", {"start": v(16.9, -29.31) * mm, "mid": v(17.05, -29.02) * mm, "end": v(16.98, -28.7) * mm});
            skPoint(sketch, "E242.visualSharp", {"position": v(11.4, -35) * mm});
            skArc(sketch, "E242.filletArc", {"start": v(12.23, -32.96) * mm, "mid": v(12.56, -33.39) * mm, "end": v(13.1, -33.26) * mm});
            skPoint(sketch, "E243.visualSharp", {"position": v(7.86, -34.73) * mm});
            skArc(sketch, "E243.filletArc", {"start": v(6.7, -34.31) * mm, "mid": v(7.2, -34.21) * mm, "end": v(7.36, -33.73) * mm});
            skPoint(sketch, "E244.visualSharp", {"position": v(12.75, -40.59) * mm});
            skArc(sketch, "E244.filletArc", {"start": v(13.12, -40.25) * mm, "mid": v(12.95, -40.6) * mm, "end": v(13.08, -40.96) * mm});
            skPoint(sketch, "E245.visualSharp", {"position": v(1.33, -32.36) * mm});
            skArc(sketch, "E245.filletArc", {"start": v(1.38, -31.96) * mm, "mid": v(1.45, -32.29) * mm, "end": v(1.7, -32.5) * mm});
            skPoint(sketch, "E246.visualSharp", {"position": v(15.57, -40.74) * mm});
            skArc(sketch, "E246.filletArc", {"start": v(15.94, -40.41) * mm, "mid": v(15.78, -40.76) * mm, "end": v(15.9, -41.12) * mm});
            skPoint(sketch, "E247.visualSharp", {"position": v(38.67, 0) * mm});
            skArc(sketch, "E247.filletArc", {"start": v(38.64, -0.1) * mm, "mid": v(38.66, 0) * mm, "end": v(38.64, 0.1) * mm});
            skPoint(sketch, "E248.visualSharp", {"position": v(-38.67, 0) * mm});
            skArc(sketch, "E248.filletArc", {"start": v(-38.64, 0.1) * mm, "mid": v(-38.66, 0) * mm, "end": v(-38.64, -0.1) * mm});
            skPoint(sketch, "E249.visualSharp", {"position": v(-28.18, 5.05) * mm});
            skArc(sketch, "E249.filletArc", {"start": v(-27.68, 5.05) * mm, "mid": v(-28.03, 4.9) * mm, "end": v(-28.18, 4.55) * mm});
            skPoint(sketch, "E250.visualSharp", {"position": v(-28.18, -2) * mm});
            skArc(sketch, "E250.filletArc", {"start": v(-28.18, -1.5) * mm, "mid": v(-28.03, -1.85) * mm, "end": v(-27.68, -2) * mm});
            skLineSegment(sketch, "E251.0", {"start": v(-26.18, 3.05) * mm, "end": v(-26.18, 0) * mm});
            skLineSegment(sketch, "E252", {"start": v(-34.53, 5.05) * mm, "end": v(-34.95, 3.05) * mm});
            skLineSegment(sketch, "E253", {"start": v(-35.6, 0) * mm, "end": v(-35.18, -2) * mm});
            skLineSegment(sketch, "E254.trimOffspring", {"start": v(12.11, 26.5) * mm, "end": v(23.7, 25.66) * mm});
            skLineSegment(sketch, "E255", {"start": v(9.6, 26.67) * mm, "end": v(10.12, 26.64) * mm});
            skLineSegment(sketch, "E256.trimOffspring", {"start": v(-11.9, 22.3) * mm, "end": v(-30.3, 23.71) * mm});
            skLineSegment(sketch, "E257.trimOffspring", {"start": v(-7.4, 21.94) * mm, "end": v(-9.9, 22.14) * mm});
            skLineSegment(sketch, "E258.trimOffspring", {"start": v(-11.83, -50) * mm, "end": v(-9.04, -50) * mm});
            skLineSegment(sketch, "E259.trimOffspring", {"start": v(-6.59, -50) * mm, "end": v(0, -50) * mm});
            skSolve(sketch);
        }
        {
            var Q0;
            Q0=makeQuery(id+"F0.imprint","IMPRINT",FACE,{"disambiguationData":[TD([[makeQuery(id+"F0.imprint","IMPRINT",EDGE,{"derivedFrom":sQuery(id+"F0.wireOp",EDGE,"E7.0")}),1.0]])]});
            var Q1;
            Q1=makeQuery(id+"F0.imprint","IMPRINT",FACE,{"disambiguationData":[TD([[makeQuery(id+"F0.imprint","IMPRINT",EDGE,{"derivedFrom":sQuery(id+"F0.wireOp",EDGE,"E45")}),1.0]])]});
            var Q2;
            Q2=makeQuery(id+"F0.imprint","IMPRINT",FACE,{"disambiguationData":[TD([[makeQuery(id+"F0.imprint","IMPRINT",EDGE,{"derivedFrom":sQuery(id+"F0.wireOp",EDGE,"E135")}),-1.0]])]});
            var Q3;
            Q3=makeQuery(id+"F0.imprint","IMPRINT",FACE,{"disambiguationData":[TD([[makeQuery(id+"F0.imprint","IMPRINT",EDGE,{"derivedFrom":sQuery(id+"F0.wireOp",EDGE,"E140.0")}),1.0]])]});
            var Q4;
            Q4=makeQuery(id+"F0.imprint","IMPRINT",FACE,{"disambiguationData":[TD([[makeQuery(id+"F0.imprint","IMPRINT",EDGE,{"derivedFrom":sQuery(id+"F0.wireOp",EDGE,"E137")}),-1.0]])]});
            var Q5;
            Q5=makeQuery(id+"F0.imprint","IMPRINT",FACE,{"disambiguationData":[TD([[makeQuery(id+"F0.imprint","IMPRINT",EDGE,{"derivedFrom":sQuery(id+"F0.wireOp",EDGE,"E201")}),-1.0]])]});
            var Q6;
            Q6=makeQuery(id+"F0.imprint","IMPRINT",FACE,{"disambiguationData":[TD([[makeQuery(id+"F0.imprint","IMPRINT",EDGE,{"derivedFrom":sQuery(id+"F0.wireOp",EDGE,"E108")}),-1.0]])]});
            var Q7;
            Q7=makeQuery(id+"F0.imprint","IMPRINT",FACE,{"disambiguationData":[TD([[makeQuery(id+"F0.imprint","IMPRINT",EDGE,{"derivedFrom":sQuery(id+"F0.wireOp",EDGE,"E3")}),1.0]])]});
            var Q8;
            Q8=makeQuery(id+"F0.imprint","IMPRINT",FACE,{"disambiguationData":[TD([[makeQuery(id+"F0.imprint","IMPRINT",EDGE,{"derivedFrom":sQuery(id+"F0.wireOp",EDGE,"E96")}),-1.0]])]});
            var Q9;
            Q9=makeQuery(id+"F0.imprint","IMPRINT",FACE,{"disambiguationData":[TD([[makeQuery(id+"F0.imprint","IMPRINT",EDGE,{"derivedFrom":sQuery(id+"F0.wireOp",EDGE,"E83.0")}),1.0]])]});
            var Q10;
            Q10=makeQuery(id+"F0.imprint","IMPRINT",FACE,{"disambiguationData":[TD([[makeQuery(id+"F0.imprint","IMPRINT",EDGE,{"derivedFrom":sQuery(id+"F0.wireOp",EDGE,"E91")}),1.0]])]});
            var Q11;
            Q11=makeQuery(id+"F0.imprint","IMPRINT",FACE,{"disambiguationData":[TD([[makeQuery(id+"F0.imprint","IMPRINT",EDGE,{"derivedFrom":sQuery(id+"F0.wireOp",EDGE,"E65")}),-1.0]])]});
            var Q12;
            Q12=makeQuery(id+"F0.imprint","IMPRINT",FACE,{"disambiguationData":[TD([[makeQuery(id+"F0.imprint","IMPRINT",EDGE,{"derivedFrom":sQuery(id+"F0.wireOp",EDGE,"E59")}),-1.0]])]});
            var Q13;
            Q13=makeQuery(id+"F0.imprint","IMPRINT",FACE,{"disambiguationData":[TD([[makeQuery(id+"F0.imprint","IMPRINT",EDGE,{"derivedFrom":sQuery(id+"F0.wireOp",EDGE,"E101")}),-1.0]])]});
            extrude(context, id + "F1", {"entities" : qUnion([Q0, Q1, Q2, Q3, Q4, Q5, Q6, Q7, Q8, Q9, Q10, Q11, Q12, Q13]), "depth" : 10 * mm, "offsetDistance" : 25 * mm});
        }
        {
            var Q0;
            Q0=makeQuery(id+"F0.imprint","IMPRINT",FACE,{"disambiguationData":[TD([[makeQuery(id+"F0.imprint","IMPRINT",EDGE,{"derivedFrom":sQuery(id+"F0.wireOp",EDGE,"E8.0")}),1.0]])]});
            var Q1;
            Q1=makeQuery(id+"F0.imprint","IMPRINT",FACE,{"disambiguationData":[TD([[makeQuery(id+"F0.imprint","IMPRINT",EDGE,{"derivedFrom":sQuery(id+"F0.wireOp",EDGE,"E114.bottom")}),-1.0]])]});
            var Q2;
            Q2=makeQuery(id+"F0.imprint","IMPRINT",FACE,{"disambiguationData":[TD([[makeQuery(id+"F0.imprint","IMPRINT",EDGE,{"derivedFrom":sQuery(id+"F0.wireOp",EDGE,"E25")}),1.0]])]});
            var Q3;
            Q3=makeQuery(id+"F0.imprint","IMPRINT",FACE,{"disambiguationData":[TD([[makeQuery(id+"F0.imprint","IMPRINT",EDGE,{"derivedFrom":sQuery(id+"F0.wireOp",EDGE,"E7.0")}),-1.0]])]});
            var Q4;
            Q4=makeQuery(id+"F0.imprint","IMPRINT",FACE,{"disambiguationData":[TD([[makeQuery(id+"F0.imprint","IMPRINT",EDGE,{"derivedFrom":sQuery(id+"F0.wireOp",EDGE,"E8.2")}),1.0]])]});
            var Q5;
            Q5=makeQuery(id+"F0.imprint","IMPRINT",FACE,{"disambiguationData":[TD([[makeQuery(id+"F0.imprint","IMPRINT",EDGE,{"derivedFrom":sQuery(id+"F0.wireOp",EDGE,"E91")}),-1.0]])]});
            var Q6;
            Q6=makeQuery(id+"F0.imprint","IMPRINT",FACE,{"disambiguationData":[TD([[makeQuery(id+"F0.imprint","IMPRINT",EDGE,{"derivedFrom":sQuery(id+"F0.wireOp",EDGE,"E96")}),1.0]])]});
            var Q7;
            Q7=makeQuery(id+"F0.imprint","IMPRINT",FACE,{"disambiguationData":[TD([[makeQuery(id+"F0.imprint","IMPRINT",EDGE,{"derivedFrom":sQuery(id+"F0.wireOp",EDGE,"E83.0")}),-1.0]])]});
            var Q8;
            Q8=makeQuery(id+"F0.imprint","IMPRINT",FACE,{"disambiguationData":[TD([[makeQuery(id+"F0.imprint","IMPRINT",EDGE,{"derivedFrom":sQuery(id+"F0.wireOp",EDGE,"E3")}),-1.0]])]});
            var Q9;
            Q9=makeQuery(id+"F0.imprint","IMPRINT",FACE,{"disambiguationData":[TD([[makeQuery(id+"F0.imprint","IMPRINT",EDGE,{"derivedFrom":sQuery(id+"F0.wireOp",EDGE,"E101")}),1.0]])]});
            var Q10;
            Q10=makeQuery(id+"F0.imprint","IMPRINT",FACE,{"disambiguationData":[TD([[makeQuery(id+"F0.imprint","IMPRINT",EDGE,{"derivedFrom":sQuery(id+"F0.wireOp",EDGE,"E131")}),1.0]])]});
            var Q11;
            Q11=makeQuery(id+"F0.imprint","IMPRINT",FACE,{"disambiguationData":[TD([[makeQuery(id+"F0.imprint","IMPRINT",EDGE,{"derivedFrom":sQuery(id+"F0.wireOp",EDGE,"E110")}),-1.0]])]});
            var Q12;
            Q12=makeQuery(id+"F0.imprint","IMPRINT",FACE,{"disambiguationData":[TD([[makeQuery(id+"F0.imprint","IMPRINT",EDGE,{"derivedFrom":sQuery(id+"F0.wireOp",EDGE,"E197")}),1.0]])]});
            var Q13;
            Q13=makeQuery(id+"F0.imprint","IMPRINT",FACE,{"disambiguationData":[TD([[makeQuery(id+"F0.imprint","IMPRINT",EDGE,{"derivedFrom":sQuery(id+"F0.wireOp",EDGE,"E201")}),1.0]])]});
            var Q14;
            Q14=makeQuery(id+"F0.imprint","IMPRINT",FACE,{"disambiguationData":[TD([[makeQuery(id+"F0.imprint","IMPRINT",EDGE,{"derivedFrom":sQuery(id+"F0.wireOp",EDGE,"E45")}),-1.0]])]});
            var Q15;
            Q15=makeQuery(id+"F0.imprint","IMPRINT",FACE,{"disambiguationData":[TD([[makeQuery(id+"F0.imprint","IMPRINT",EDGE,{"derivedFrom":sQuery(id+"F0.wireOp",EDGE,"E145.MirrorCS")}),1.0]])]});
            var Q16;
            Q16=makeQuery(id+"F0.imprint","IMPRINT",FACE,{"disambiguationData":[TD([[makeQuery(id+"F0.imprint","IMPRINT",EDGE,{"derivedFrom":sQuery(id+"F0.wireOp",EDGE,"E156")}),1.0]])]});
            var Q17;
            Q17=makeQuery(id+"F0.imprint","IMPRINT",FACE,{"disambiguationData":[TD([[makeQuery(id+"F0.imprint","IMPRINT",EDGE,{"derivedFrom":sQuery(id+"F0.wireOp",EDGE,"E59")}),1.0]])]});
            var Q18;
            Q18=makeQuery(id+"F0.imprint","IMPRINT",FACE,{"disambiguationData":[TD([[makeQuery(id+"F0.imprint","IMPRINT",EDGE,{"derivedFrom":sQuery(id+"F0.wireOp",EDGE,"E78")}),-1.0]])]});
            var Q19;
            Q19=makeQuery(id+"F0.imprint","IMPRINT",FACE,{"disambiguationData":[TD([[makeQuery(id+"F0.imprint","IMPRINT",EDGE,{"derivedFrom":sQuery(id+"F0.wireOp",EDGE,"E65")}),1.0]])]});
            var Q20;
            Q20=makeQuery(id+"F0.imprint","IMPRINT",FACE,{"disambiguationData":[TD([[makeQuery(id+"F0.imprint","IMPRINT",EDGE,{"derivedFrom":sQuery(id+"F0.wireOp",EDGE,"E135")}),1.0]])]});
            var Q21;
            Q21=makeQuery(id+"F0.imprint","IMPRINT",FACE,{"disambiguationData":[TD([[makeQuery(id+"F0.imprint","IMPRINT",EDGE,{"derivedFrom":sQuery(id+"F0.wireOp",EDGE,"E140.0")}),-1.0]])]});
            var Q22;
            Q22=makeQuery(id+"F0.imprint","IMPRINT",FACE,{"disambiguationData":[TD([[makeQuery(id+"F0.imprint","IMPRINT",EDGE,{"derivedFrom":sQuery(id+"F0.wireOp",EDGE,"E137")}),1.0]])]});
            var Q23;
            Q23=makeQuery(id+"F0.imprint","IMPRINT",FACE,{"disambiguationData":[TD([[makeQuery(id+"F0.imprint","IMPRINT",EDGE,{"derivedFrom":sQuery(id+"F0.wireOp",EDGE,"E103")}),1.0]])]});
            var Q24;
            Q24=makeQuery(id+"F0.imprint","IMPRINT",FACE,{"disambiguationData":[TD([[makeQuery(id+"F0.imprint","IMPRINT",EDGE,{"derivedFrom":sQuery(id+"F0.wireOp",EDGE,"E9")}),1.0]])]});
            var Q25;
            Q25=makeQuery(id+"F0.imprint","IMPRINT",FACE,{"disambiguationData":[TD([[makeQuery(id+"F0.imprint","IMPRINT",EDGE,{"derivedFrom":sQuery(id+"F0.wireOp",EDGE,"E50")}),1.0]])]});
            var Q26;
            Q26=makeQuery(id+"F0.imprint","IMPRINT",FACE,{"disambiguationData":[TD([[makeQuery(id+"F0.imprint","IMPRINT",EDGE,{"derivedFrom":sQuery(id+"F0.wireOp",EDGE,"E54")}),-1.0]])]});
            extrude(context, id + "F2", {"entities" : qUnion([Q0, Q1, Q2, Q3, Q4, Q5, Q6, Q7, Q8, Q9, Q10, Q11, Q12, Q13, Q14, Q15, Q16, Q17, Q18, Q19, Q20, Q21, Q22, Q23, Q24, Q25, Q26]), "depth" : 2 * mm, "offsetDistance" : 25 * mm});
        }
    });
